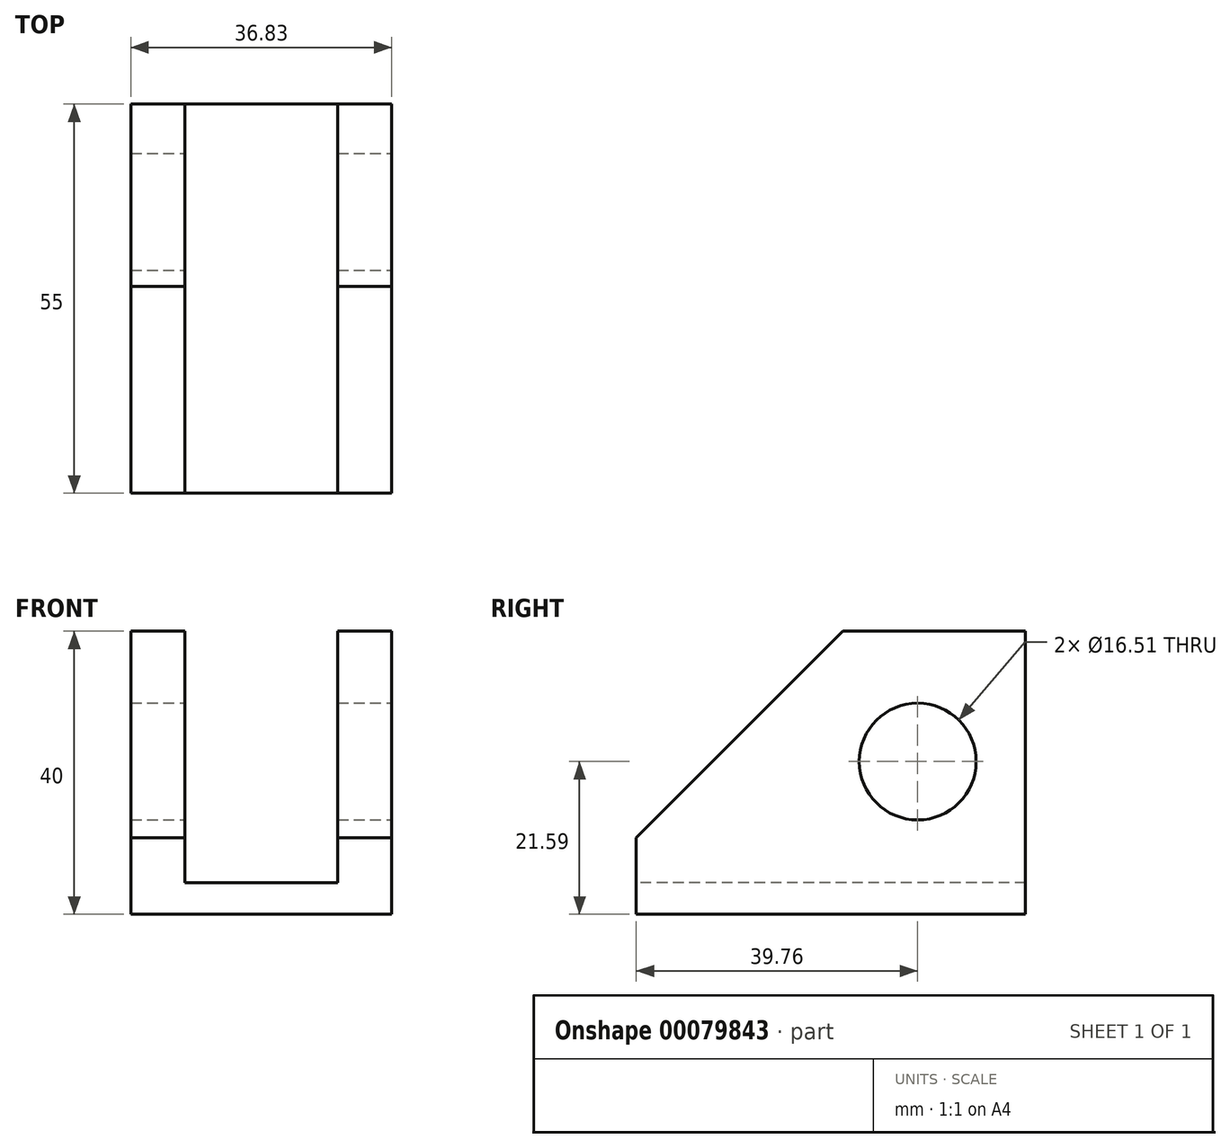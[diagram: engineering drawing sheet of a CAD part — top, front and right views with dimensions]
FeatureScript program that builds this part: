
annotation { "Feature Type Name" : "Feature", "Feature Type Description" : "" }
export const myFeature = defineFeature(function(context is Context, id is Id, definition is map)
    precondition{}
    {
        {
            var Q0;
            Q0=qCreatedBy(makeId("Front.planeOp"),FACE);
            var sketch = newSketch(context, id + "F0", { "sketchPlane" : qUnion([Q0])});
            skLineSegment(sketch, "E0.bottom", {"start": v(0, 0) * mm, "end": v(36.83, 0) * mm});
            skLineSegment(sketch, "E0.top", {"start": v(0, 40) * mm, "end": v(36.83, 40) * mm});
            skLineSegment(sketch, "E0.left", {"start": v(0, 0) * mm, "end": v(0, 40) * mm});
            skLineSegment(sketch, "E0.right", {"start": v(36.83, 0) * mm, "end": v(36.83, 40) * mm});
            skSolve(sketch);
        }
        {
            var Q0;
            Q0=makeQuery(id+"F0.imprint","IMPRINT",FACE,{"disambiguationData":[TD([[makeQuery(id+"F0.imprint","IMPRINT",EDGE,{"derivedFrom":sQuery(id+"F0.wireOp",EDGE,"E0.bottom")}),1.0]])]});
            extrude(context, id + "F1", {"entities" : qUnion([Q0]), "depth" : 55 * mm});
        }
        {
            var Q0;
            Q0=makeQuery(id+"F1.opExtrude","CAP_EDGE",EDGE,{"disambiguationData":[OSD([sQuery(id+"F0.wireOp",EDGE,"E0.top")])],"isStart":false});
            chamfer(context, id + "F2", {"entities" : qUnion([Q0]), "width" : 29.2 * mm, "tangentPropagation" : true});
        }
        {
            var Q0;
            Q0=makeQuery(id+"F1.opExtrude","SWEPT_FACE",FACE,{"disambiguationData":[OSD([sQuery(id+"F0.wireOp",EDGE,"E0.top")])]});
            var sketch = newSketch(context, id + "F3", { "sketchPlane" : qUnion([Q0])});
            skPoint(sketch, "E1", {"position": v(7.62, 0) * mm});
            skPoint(sketch, "E2", {"position": v(29.2, 0) * mm});
            skPoint(sketch, "E3", {"position": v(36.83, 0) * mm});
            skLineSegment(sketch, "E4", {"start": v(7.62, 0) * mm, "end": v(29.2, 0) * mm});
            skLineSegment(sketch, "E5", {"start": v(29.2, 0) * mm, "end": v(29.2, -55.35) * mm});
            skLineSegment(sketch, "E6", {"start": v(7.62, 0) * mm, "end": v(7.62, -55.68) * mm});
            skLineSegment(sketch, "E7", {"start": v(7.62, -55.68) * mm, "end": v(29.2, -55.35) * mm});
            skSolve(sketch);
        }
        {
            var Q0;
            {var subQ0=sQuery(id+"F3.wireOp",EDGE,"E4");Q0=makeQuery(id+"F3.imprint","IMPRINT",FACE,{"disambiguationData":[TD([[makeQuery(id+"F3.imprint","IMPRINT",EDGE,{"derivedFrom":subQ0}),-1.0]])]});}
            var Q1;
            {var subQ0=sQuery(id+"F3.wireOp",EDGE,"E7");Q1=makeQuery(id+"F3.imprint","IMPRINT",FACE,{"disambiguationData":[TD([[makeQuery(id+"F3.imprint","IMPRINT",EDGE,{"derivedFrom":subQ0}),1.0]])]});}
            extrude(context, id + "F4", {"entities" : qUnion([Q0, Q1]), "operationType" : NewBodyOperationType.REMOVE, "oppositeDirection" : true, "depth" : 35.56 * mm});
        }
        {
            var Q0;
            Q0=makeQuery(id+"F1.opExtrude","SWEPT_FACE",FACE,{"disambiguationData":[OSD([sQuery(id+"F0.wireOp",EDGE,"E0.right")])]});
            var sketch = newSketch(context, id + "F5", { "sketchPlane" : qUnion([Q0])});
            skPoint(sketch, "E8", {"position": v(-15.24, 21.59) * mm});
            skCircle(sketch, "E9", {"center": v(-15.24, 21.59) * mm, "radius": 8.26 * mm});
            skSolve(sketch);
        }
        {
            var Q0;
            Q0=makeQuery(id+"F5.imprint","IMPRINT",FACE,{"disambiguationData":[TD([[makeQuery(id+"F5.imprint","IMPRINT",EDGE,{"derivedFrom":sQuery(id+"F5.wireOp",EDGE,"E9")}),1.0]])]});
            extrude(context, id + "F6", {"entities" : qUnion([Q0]), "operationType" : NewBodyOperationType.REMOVE, "oppositeDirection" : true, "depth" : 50.8 * mm});
        }
    });
